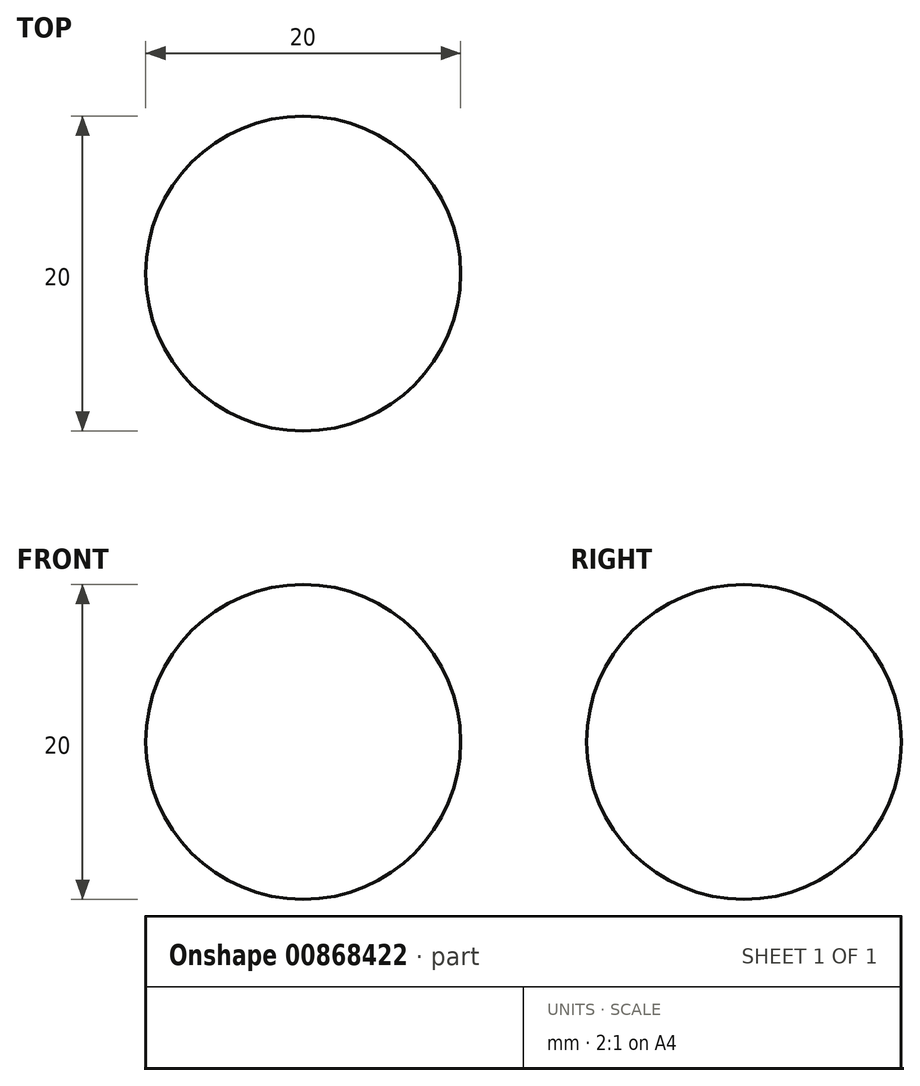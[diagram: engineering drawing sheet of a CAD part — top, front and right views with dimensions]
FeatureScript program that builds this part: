
annotation { "Feature Type Name" : "Feature", "Feature Type Description" : "" }
export const myFeature = defineFeature(function(context is Context, id is Id, definition is map)
    precondition{}
    {
        {
            var Q0;
            Q0=qCreatedBy(makeId("Top.planeOp"),FACE);
            var sketch = newSketch(context, id + "F0", { "sketchPlane" : qUnion([Q0])});
            skCircle(sketch, "E0", {"center": v(0, 0) * mm, "radius": 10 * mm});
            skLineSegment(sketch, "E1", {"start": v(0, 0) * mm, "end": v(0, 10) * mm});
            skLineSegment(sketch, "E2", {"start": v(0, 10) * mm, "end": v(0, 5) * mm, "construction": true});
            skLineSegment(sketch, "E3", {"start": v(0, 10) * mm, "end": v(0, -10) * mm});
            skSolve(sketch);
        }
        {
            var Q0;
            {var subQ0=sQuery(id+"F0.wireOp",EDGE,"E3");var subQ4=makeQuery(id+"F0.imprint","IMPRINT",VERTEX,{"derivedFrom":subQ0});Q0=makeQuery(id+"F0.imprint","IMPRINT",FACE,{"disambiguationData":[TD([[makeQuery(id+"F0.imprint","IMPRINT",EDGE,{"disambiguationData":[TD([[subQ4,1.0]])],"derivedFrom":subQ0}),-1.0]])]});}
            var Q1;
            Q1=sQuery(id+"F0.wireOp",EDGE,"E3");
            revolve(context, id + "F1", {"surfaceOperationType" : NewSurfaceOperationType.NEW, "entities" : qUnion([Q0]), "axis" : qUnion([Q1]), "revolveType" : RevolveType.FULL});
        }
    });
